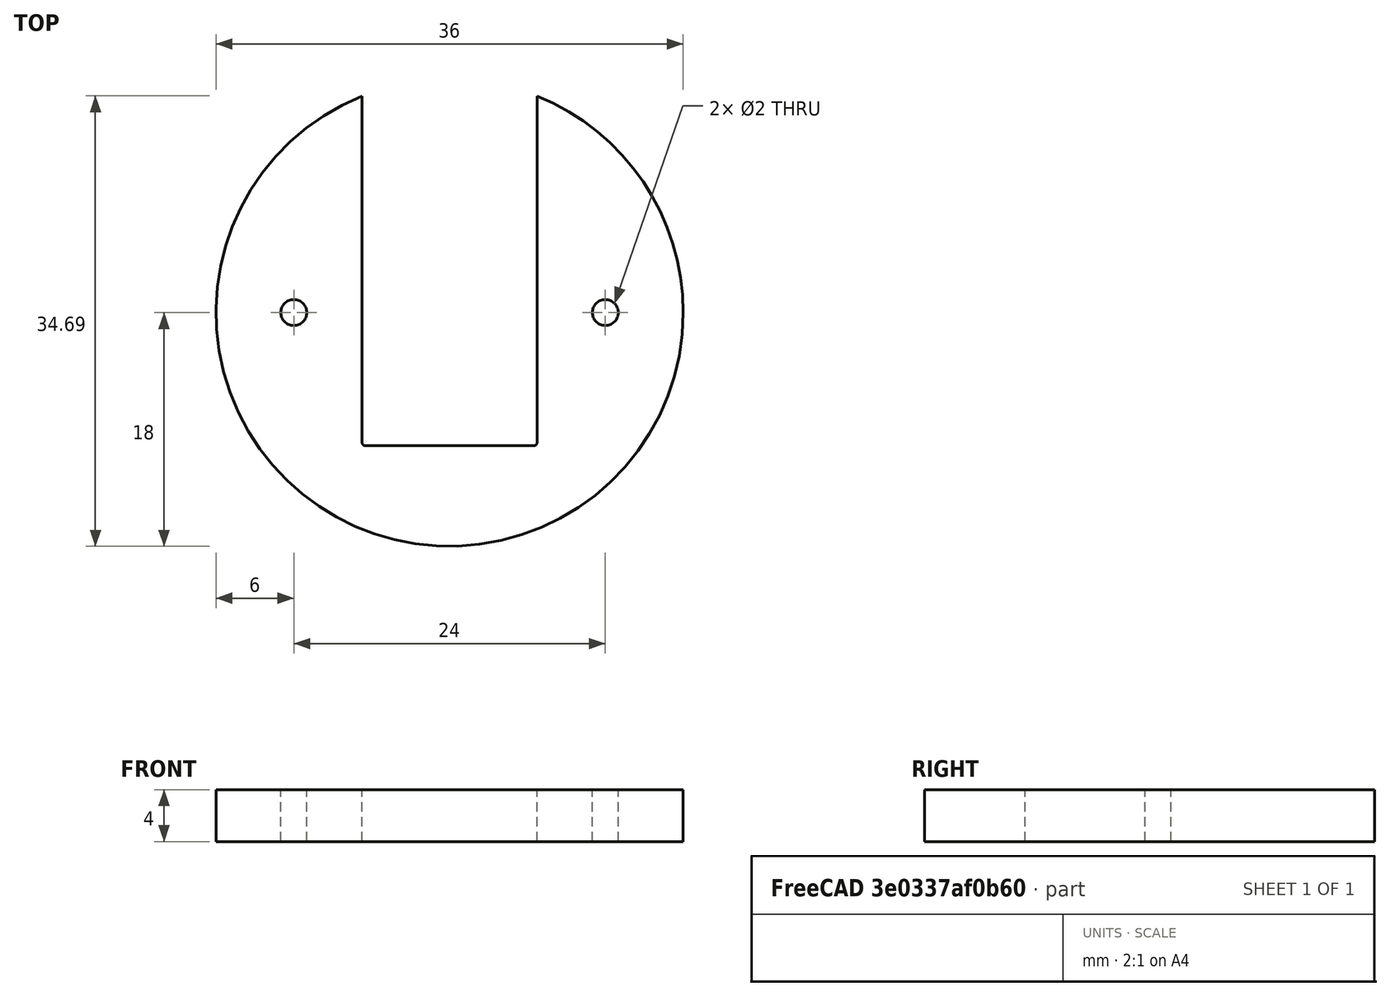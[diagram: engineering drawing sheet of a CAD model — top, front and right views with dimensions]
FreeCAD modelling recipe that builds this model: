
FCSTD DOCUMENT  (FreeCAD 0.16R6712 (Git))
Label: Soporte servo 13 x 28
License: CreativeCommons Attribution
LicenseURL: http://creativecommons.org/licenses/by/4.0/
objects: Part::Cylinder×2, Part::Box×1, Part::Offset×1, Part::Mirroring×1, Part::MultiFuse×1, Part::Cut×1
note: 7 computed .brp shape members not serialized (recipe doc carries the construction recipe); baked Part::Feature solids carry a one-line shape summary decoded from their .brp

FEATURE [Part::Cylinder] Cylinder  label="Cilindro base"
  Angle = 360
  Height = 4
  Radius = 18
FEATURE [Part::Box] Box  label="Cubo hueco servo 13*28"
  Height = 10
  Length = 13
  Placement = pos=(-6.5,-10,-2) rot=(0,0,1;0rad)
  Width = 28
FEATURE [Part::Offset] Offset  label=" Offset hueco servo 13*28"
  Fill = false
  Intersection = false
  Join = 0
  Mode = 0
  SelfIntersection = false
  Source = -> Box
  Value = 0.25
FEATURE [Part::Cylinder] Cylinder001  label="Cilindro paso chincheta"
  Angle = 360
  Height = 10
  Placement = pos=(-12,0,-2) rot=(0,0,1;0rad)
  Radius = 1
FEATURE [Part::Mirroring] Part__Mirroring  label="Cilindro paso chincheta (Mirror #1)"
  Base = (0,0,0)
  Normal = (1,0,0)
  Source = -> Cylinder001
FEATURE [Part::MultiFuse] Fusion  label="Fusion huecos"
  Shapes = -> [Offset,Part__Mirroring,Cylinder001]
FEATURE [Part::Cut] Cut  label="Soporte Servo 13 x 28"
  Base = -> Cylinder
  Tool = -> Fusion
